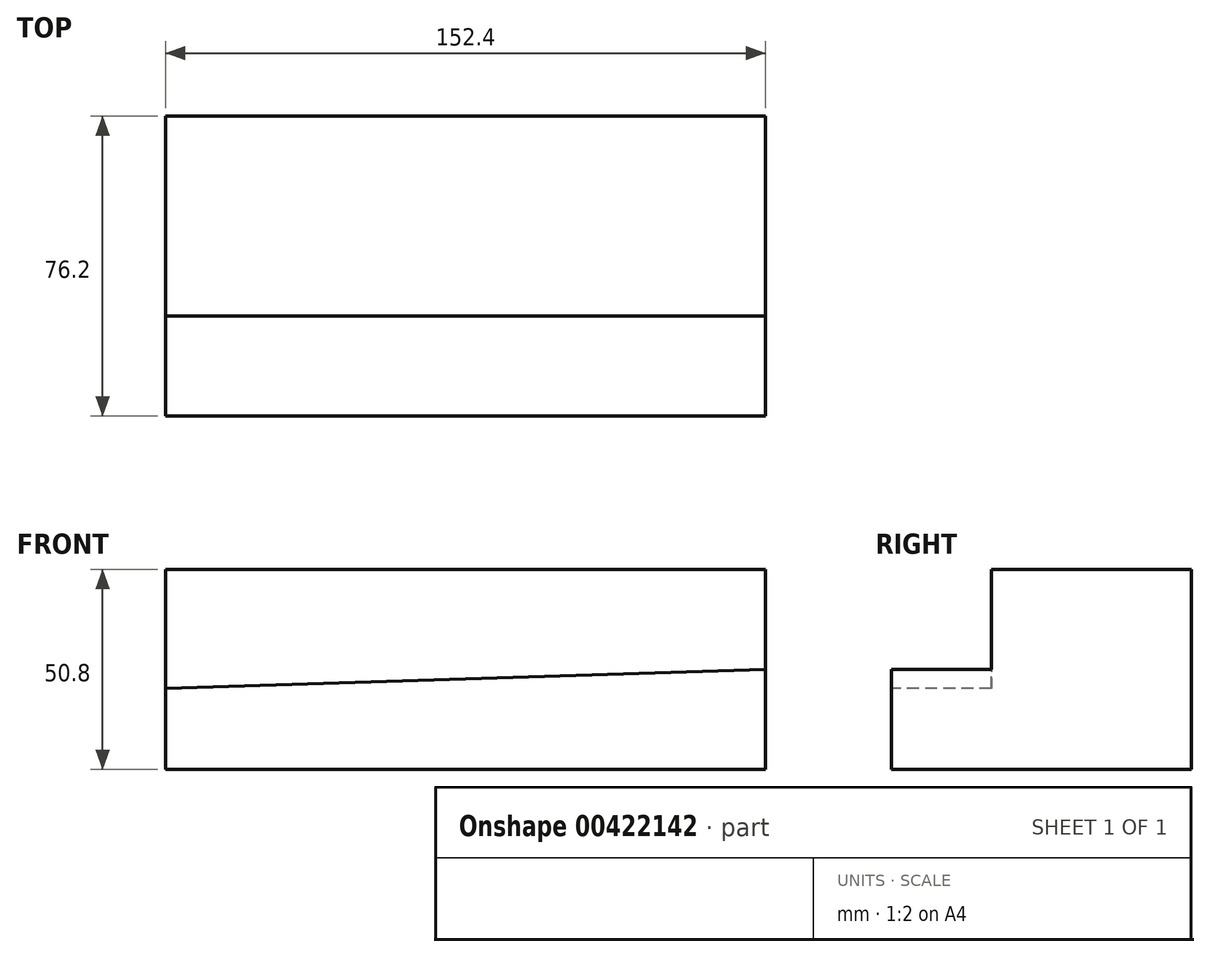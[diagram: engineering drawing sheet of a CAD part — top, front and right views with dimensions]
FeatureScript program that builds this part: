
annotation { "Feature Type Name" : "Feature", "Feature Type Description" : "" }
export const myFeature = defineFeature(function(context is Context, id is Id, definition is map)
    precondition{}
    {
        {
            var Q0;
            Q0=qCreatedBy(makeId("Front.planeOp"),FACE);
            var sketch = newSketch(context, id + "F0", { "sketchPlane" : qUnion([Q0])});
            skLineSegment(sketch, "E0", {"start": v(0, 0) * mm, "end": v(152.4, 0) * mm});
            skLineSegment(sketch, "E1", {"start": v(152.4, 0) * mm, "end": v(152.4, 50.8) * mm});
            skLineSegment(sketch, "E2", {"start": v(152.4, 50.8) * mm, "end": v(0, 50.8) * mm});
            skLineSegment(sketch, "E3", {"start": v(0, 50.8) * mm, "end": v(0, 0) * mm});
            skSolve(sketch);
        }
        {
            var Q0;
            Q0 = qSketchRegion(id + "F0", true);
            extrude(context, id + "F1", {"entities" : qUnion([Q0]), "depth" : 76.2 * mm});
        }
        {
            var Q0;
            Q0=makeQuery(id+"F1.opExtrude","CAP_FACE",FACE,{"disambiguationData":[OSD([sQuery(id+"F0.wireOp",EDGE,"E0"),sQuery(id+"F0.wireOp",EDGE,"E1"),sQuery(id+"F0.wireOp",EDGE,"E2"),sQuery(id+"F0.wireOp",EDGE,"E3")])],"isStart":false});
            var sketch = newSketch(context, id + "F2", { "sketchPlane" : qUnion([Q0])});
            skLineSegment(sketch, "E4", {"start": v(0, 20.57) * mm, "end": v(152.4, 25.4) * mm});
            skLineSegment(sketch, "E5", {"start": v(152.4, 25.4) * mm, "end": v(152.4, 50.8) * mm});
            skLineSegment(sketch, "E6", {"start": v(152.4, 50.8) * mm, "end": v(0, 50.8) * mm});
            skLineSegment(sketch, "E7", {"start": v(-0.53, 48.25) * mm, "end": v(0, 20.57) * mm});
            skSolve(sketch);
        }
        {
            var Q0;
            Q0 = qSketchRegion(id + "F2", true);
            var Q1;
            {var subQ0=sQuery(id+"F2.wireOp",EDGE,"E4");Q1=makeQuery(id+"F2.imprint","IMPRINT",FACE,{"disambiguationData":[TD([[makeQuery(id+"F2.imprint","IMPRINT",EDGE,{"derivedFrom":subQ0}),1.0]])]});}
            extrude(context, id + "F3", {"entities" : qUnion([Q0, Q1]), "operationType" : NewBodyOperationType.REMOVE, "oppositeDirection" : true, "depth" : 25.4 * mm});
        }
    });
